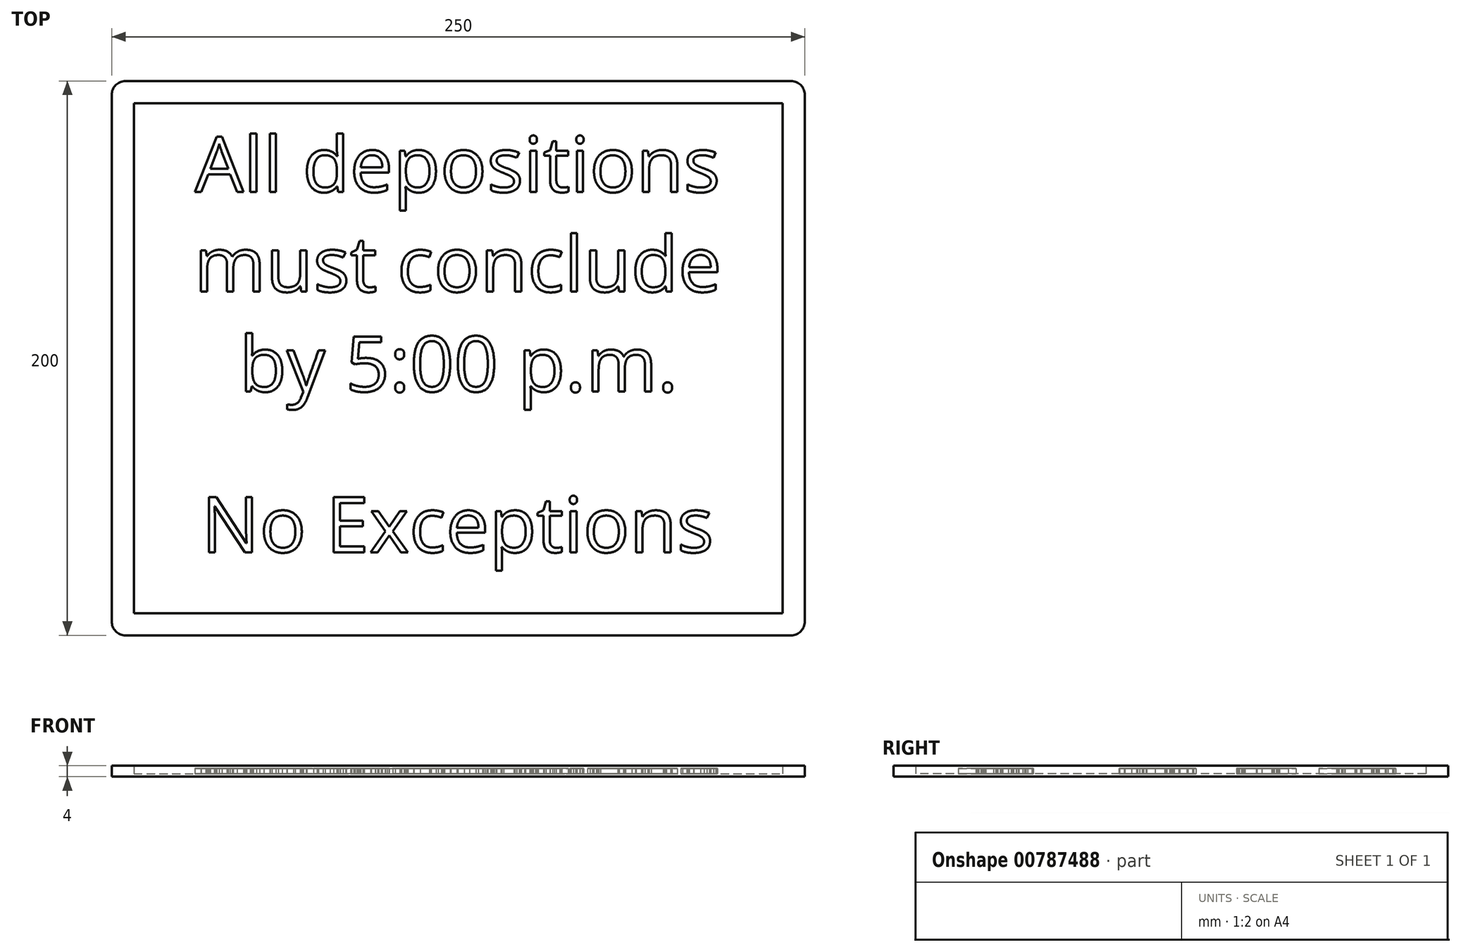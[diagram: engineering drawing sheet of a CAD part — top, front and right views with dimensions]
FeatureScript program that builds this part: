
annotation { "Feature Type Name" : "Feature", "Feature Type Description" : "" }
export const myFeature = defineFeature(function(context is Context, id is Id, definition is map)
    precondition{}
    {
        {
            var Q0;
            Q0=qCreatedBy(makeId("Top.planeOp"),FACE);
            var sketch = newSketch(context, id + "F0", { "sketchPlane" : qUnion([Q0])});
            skLineSegment(sketch, "E0.bottom", {"start": v(-125, 125) * mm, "end": v(125, 125) * mm});
            skLineSegment(sketch, "E0.top", {"start": v(-125, -75) * mm, "end": v(125, -75) * mm});
            skLineSegment(sketch, "E0.left", {"start": v(-125, 125) * mm, "end": v(-125, -75) * mm});
            skLineSegment(sketch, "E0.right", {"start": v(125, 125) * mm, "end": v(125, -75) * mm});
            skSolve(sketch);
        }
        {
            var Q0;
            Q0 = qSketchRegion(id + "F0", true);
            extrude(context, id + "F1", {"entities" : qUnion([Q0]), "depth" : 1 * mm, "offsetDistance" : 25 * mm});
        }
        {
            var Q0;
            Q0=makeQuery(id+"F1.opExtrude","CAP_FACE",FACE,{"disambiguationData":[OSD([sQuery(id+"F0.wireOp",EDGE,"E0.bottom"),sQuery(id+"F0.wireOp",EDGE,"E0.top"),sQuery(id+"F0.wireOp",EDGE,"E0.left"),sQuery(id+"F0.wireOp",EDGE,"E0.right")])],"isStart":false});
            var sketch = newSketch(context, id + "F2", { "sketchPlane" : qUnion([Q0])});
            skText(sketch, "E1", { "text": "All depositions ", "fontName": "OpenSans-Regular.ttf"});
            skText(sketch, "E2", { "text": "must conclude ", "fontName": "OpenSans-Regular.ttf"});
            skText(sketch, "E3", { "text": "by 5:00 p.m. ", "fontName": "OpenSans-Regular.ttf"});
            skText(sketch, "E4", { "text": "No Exceptions", "fontName": "OpenSans-Regular.ttf"});
            const initialGuessF2  = {"E1": [-0.09499, 0.085, 1, 0, 0.02], "E2": [-0.09523, 0.049, 1, 0, 0.02], "E3": [-0.07894, 0.013, 1, 0, 0.02], "E4": [-0.0926, -0.045, 1, 0, 0.02]};
            skSetInitialGuess(sketch, initialGuessF2);
            skSolve(sketch);
        }
        {
            var Q0;
            Q0 = qSketchRegion(id + "F2", true);
            extrude(context, id + "F3", {"entities" : qUnion([Q0]), "operationType" : NewBodyOperationType.ADD, "depth" : 2 * mm, "offsetDistance" : 25 * mm});
        }
        {
            var Q0;
            {var subQ0=sQuery(id+"F0.wireOp",EDGE,"E0.right");var subQ1=sQuery(id+"F0.wireOp",EDGE,"E0.left");var subQ2=sQuery(id+"F0.wireOp",EDGE,"E0.top");var subQ3=sQuery(id+"F0.wireOp",EDGE,"E0.bottom");Q0=makeQuery(id+"F3.boolean.opBoolean","SPLIT",FACE,{"disambiguationData":[TD([makeQuery(id+"F1.opExtrude","SWEPT_FACE",FACE,{"disambiguationData":[OSD([subQ3])]})])],"derivedFrom":makeQuery(id+"F1.opExtrude","CAP_FACE",FACE,{"disambiguationData":[OSD([subQ3,subQ2,subQ1,subQ0])],"isStart":false})});}
            var sketch = newSketch(context, id + "F4", { "sketchPlane" : qUnion([Q0])});
            skLineSegment(sketch, "E5.0", {"start": v(-117, 117) * mm, "end": v(-117, -67) * mm});
            skLineSegment(sketch, "E5.1", {"start": v(-117, 117) * mm, "end": v(117, 117) * mm});
            skLineSegment(sketch, "E5.2", {"start": v(117, 117) * mm, "end": v(117, -67) * mm});
            skLineSegment(sketch, "E5.3", {"start": v(-117, -67) * mm, "end": v(117, -67) * mm});
            skSolve(sketch);
        }
        {
            var Q0;
            Q0=makeQuery(id+"F4.imprint","IMPRINT",FACE,{"disambiguationData":[TD([[makeQuery(id+"F4.imprint","IMPRINT",EDGE,{"derivedFrom":sQuery(id+"F4.wireOp",EDGE,"E5.0")}),-1.0]])]});
            extrude(context, id + "F5", {"entities" : qUnion([Q0]), "operationType" : NewBodyOperationType.ADD, "depth" : 3 * mm, "offsetDistance" : 25 * mm});
        }
        {
            var Q0;
            {var subQ0=sQuery(id+"F0.wireOp",EDGE,"E0.left");var subQ1=sQuery(id+"F0.wireOp",EDGE,"E0.top");Q0=makeQuery(id+"F5.boolean.opBoolean","MERGE",EDGE,{"derivedFrom":[makeQuery(id+"F1.opExtrude","SWEPT_EDGE",EDGE,{"disambiguationData":[OSD([subQ1,subQ0])]}),makeQuery(id+"F5.opExtrude","SWEPT_EDGE",EDGE,{"disambiguationData":[OSD([subQ1,subQ0])]})]});}
            var Q1;
            {var subQ0=sQuery(id+"F0.wireOp",EDGE,"E0.left");var subQ1=sQuery(id+"F0.wireOp",EDGE,"E0.bottom");Q1=makeQuery(id+"F5.boolean.opBoolean","MERGE",EDGE,{"derivedFrom":[makeQuery(id+"F1.opExtrude","SWEPT_EDGE",EDGE,{"disambiguationData":[OSD([subQ1,subQ0])]}),makeQuery(id+"F5.opExtrude","SWEPT_EDGE",EDGE,{"disambiguationData":[OSD([subQ1,subQ0])]})]});}
            var Q2;
            {var subQ0=sQuery(id+"F0.wireOp",EDGE,"E0.right");var subQ1=sQuery(id+"F0.wireOp",EDGE,"E0.bottom");Q2=makeQuery(id+"F5.boolean.opBoolean","MERGE",EDGE,{"derivedFrom":[makeQuery(id+"F1.opExtrude","SWEPT_EDGE",EDGE,{"disambiguationData":[OSD([subQ1,subQ0])]}),makeQuery(id+"F5.opExtrude","SWEPT_EDGE",EDGE,{"disambiguationData":[OSD([subQ1,subQ0])]})]});}
            var Q3;
            {var subQ0=sQuery(id+"F0.wireOp",EDGE,"E0.right");var subQ1=sQuery(id+"F0.wireOp",EDGE,"E0.top");Q3=makeQuery(id+"F5.boolean.opBoolean","MERGE",EDGE,{"derivedFrom":[makeQuery(id+"F1.opExtrude","SWEPT_EDGE",EDGE,{"disambiguationData":[OSD([subQ1,subQ0])]}),makeQuery(id+"F5.opExtrude","SWEPT_EDGE",EDGE,{"disambiguationData":[OSD([subQ1,subQ0])]})]});}
            fillet(context, id + "F6", {"entities" : qUnion([Q0, Q1, Q2, Q3]), "radius" : 5 * mm, "tangentPropagation" : true, "allowEdgeOverflow" : false});
        }
    });
